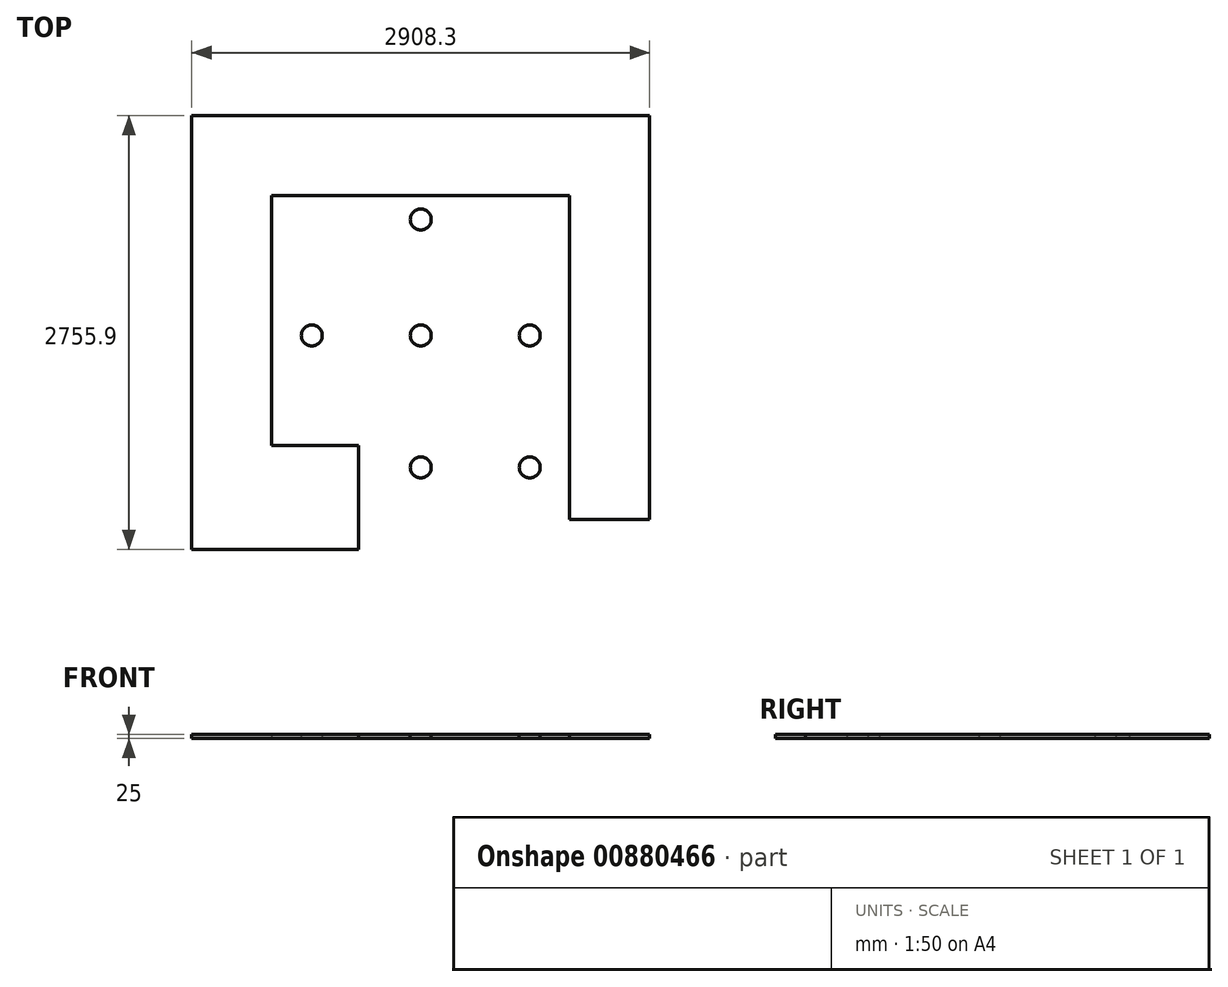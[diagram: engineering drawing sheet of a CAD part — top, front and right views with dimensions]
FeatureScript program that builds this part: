
annotation { "Feature Type Name" : "Feature", "Feature Type Description" : "" }
export const myFeature = defineFeature(function(context is Context, id is Id, definition is map)
    precondition{}
    {
        {
            var Q0;
            Q0=qCreatedBy(makeId("Top.planeOp"),FACE);
            var sketch = newSketch(context, id + "F0", { "sketchPlane" : qUnion([Q0])});
            skLineSegment(sketch, "E0", {"start": v(0, 0) * mm, "end": v(-1892.3, 0) * mm});
            skLineSegment(sketch, "E1", {"start": v(-1892.3, 0) * mm, "end": v(-1892.3, -1587.5) * mm});
            skLineSegment(sketch, "E2", {"start": v(-1892.3, -1587.5) * mm, "end": v(-1339.85, -1587.5) * mm});
            skLineSegment(sketch, "E3", {"start": v(-1339.85, -1587.5) * mm, "end": v(-1339.85, -2247.9) * mm});
            skLineSegment(sketch, "E4", {"start": v(0, -2057.4) * mm, "end": v(0, 0) * mm});
            skCircle(sketch, "E5", {"center": v(-946.15, -152.4) * mm, "radius": 66.68 * mm});
            skCircle(sketch, "E6", {"center": v(-1638.3, -889) * mm, "radius": 66.68 * mm});
            skCircle(sketch, "E7", {"center": v(-254, -889) * mm, "radius": 66.68 * mm});
            skCircle(sketch, "E8", {"center": v(-254, -1727.2) * mm, "radius": 66.68 * mm});
            skCircle(sketch, "E9", {"center": v(-946.15, -1727.2) * mm, "radius": 66.68 * mm});
            skLineSegment(sketch, "E10", {"start": v(-1339.85, -2247.9) * mm, "end": v(-2400.3, -2247.9) * mm});
            skLineSegment(sketch, "E11", {"start": v(-2400.3, -2247.9) * mm, "end": v(-2400.3, 508) * mm});
            skLineSegment(sketch, "E12", {"start": v(-2400.3, 508) * mm, "end": v(508, 508) * mm});
            skLineSegment(sketch, "E13", {"start": v(508, 508) * mm, "end": v(508, -2057.4) * mm});
            skLineSegment(sketch, "E14", {"start": v(508, -2057.4) * mm, "end": v(0, -2057.4) * mm});
            skCircle(sketch, "E15", {"center": v(-946.15, -889) * mm, "radius": 66.68 * mm});
            skSolve(sketch);
        }
        {
            var Q0;
            Q0 = qSketchRegion(id + "F0", true);
            extrude(context, id + "F1", {"entities" : qUnion([Q0]), "depth" : 25 * mm, "offsetDistance" : 25 * mm});
        }
    });
